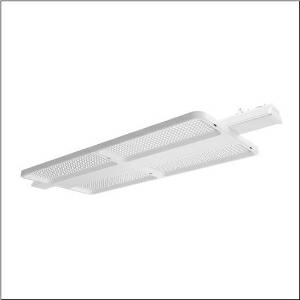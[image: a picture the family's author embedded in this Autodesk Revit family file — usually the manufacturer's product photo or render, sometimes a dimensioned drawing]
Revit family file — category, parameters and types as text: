
# Revit family: highbay_21_fur_licross_r__tragschiene_maxi_52hn11db4qla_e1de
name_source: partatom
category: Lighting Fixtures
units: mm (PartAtom-declared; Revit-internal decimal feet)

## family parameters
Cut with Voids When Loaded = No
Host = Face
Light Source = No
Part Type = Normal
Room Calculation Point = No
Round Connector Dimension = Use Diameter
Shared = No

## types (1)
- --- (1 x LED, 38000 lm, 197.7 W, 4000K)
    Apparent Load = 198 VA
    CIE Flux Codes = 89 97 99 100 100
    Color Rendering = 80
    Color Temperature = 4000K
    Default Elevation = 1800 mm
    Description = Highbay 21 for Licross® trunking rail maxi, high bay luminaire, primary light control with lens, of PMMA, primary optical cover: cover, of PMMA, light emission: direct distribution, primary light characteristic: symmetric, LED, rated luminous flux: 38.000lm, luminous efficacy: 192lm/W, light colour: 840, colour temperature: 4000K, control gear: DALI 2, with plug, 5-pole, with phase selection, mains connection: 230..240V, AC, 50/60Hz, rated input power: 197.7W, housing frame, of high-performance plastic PA6, matt traffic white (RAL 9016), length: 1.250mm, width: 442mm, height: 71mm, lever catch, fixing on rail side, of steel, galvanised, white, blank cover, of PC/ABS, traffic white (RAL 9016), protection rating (complete): IP64, insulation class (complete): insulation class I (protective earthing), certification: CE, ENEC, VDE, UKCA, protection symbol: D, impact resistance: IK07, permissible operating ambient temperature: -40..+55°C, LABS conformity tested according to VDMA 24364:2018-05, corresponds to IFS (International Featured Standards) requirements for safety and quality in the food industry, packaging unit: 1 piece
    Height = 72 mm  [stored 0.23622 ft]
    Lamp = 1 x LED
    Lamp Light Flux = 38000 lm
    Lamp Power = 197.7 W
    Lamp count = 1
    Length = 946 mm
    Luminous efficacy = 192 lm/W
    Manufacturer = Siteco
    ModVariant = No
    Model = 52HN11DB4QLA
    Mounting Place = Ceiling
    Mounting Type = Pendant
    Number of Poles = 1
    OnlyDefault = Yes
    Power Factor = 1
    Product Name = Highbay 21 für Licross® Tragschiene maxi
    Product group = high bay luminaire
    ProductGroupID = 901
    Protection Class = Protection class I
    Protection Degree = IP 64
    RLX_Detail_Level = 1
    RLX_Emergency_Light_Flux = 0 lm
    RLX_Emergency_Type = 0
    RLX_Emergency_Type_DB = No
    RlxData = <blob elided: 24893 chars, md5=15444d7e>
    Socket = socket
    Standby Power = 0 W
    System Light Flux = 38000 lm
    System Power = 198 W
    Type Comments = factory setting: luminous flux: 100 % | dim-lin: 254 | 918 mA
    Type Image = l_1361711.jpg
    URL = http://relux.com
    VarID = @adj_000043
    Voltage = 0 V
    Weight = 0.00 kg
    Width = 442 mm

note: [stored X ft] marks values corroborated as IEEE doubles in the binary element streams (Revit-internal decimal feet)

## geometry (parser evidence)
native form markers: Blend x4, Sweep x10
no freeform markers — native parametric forms only
